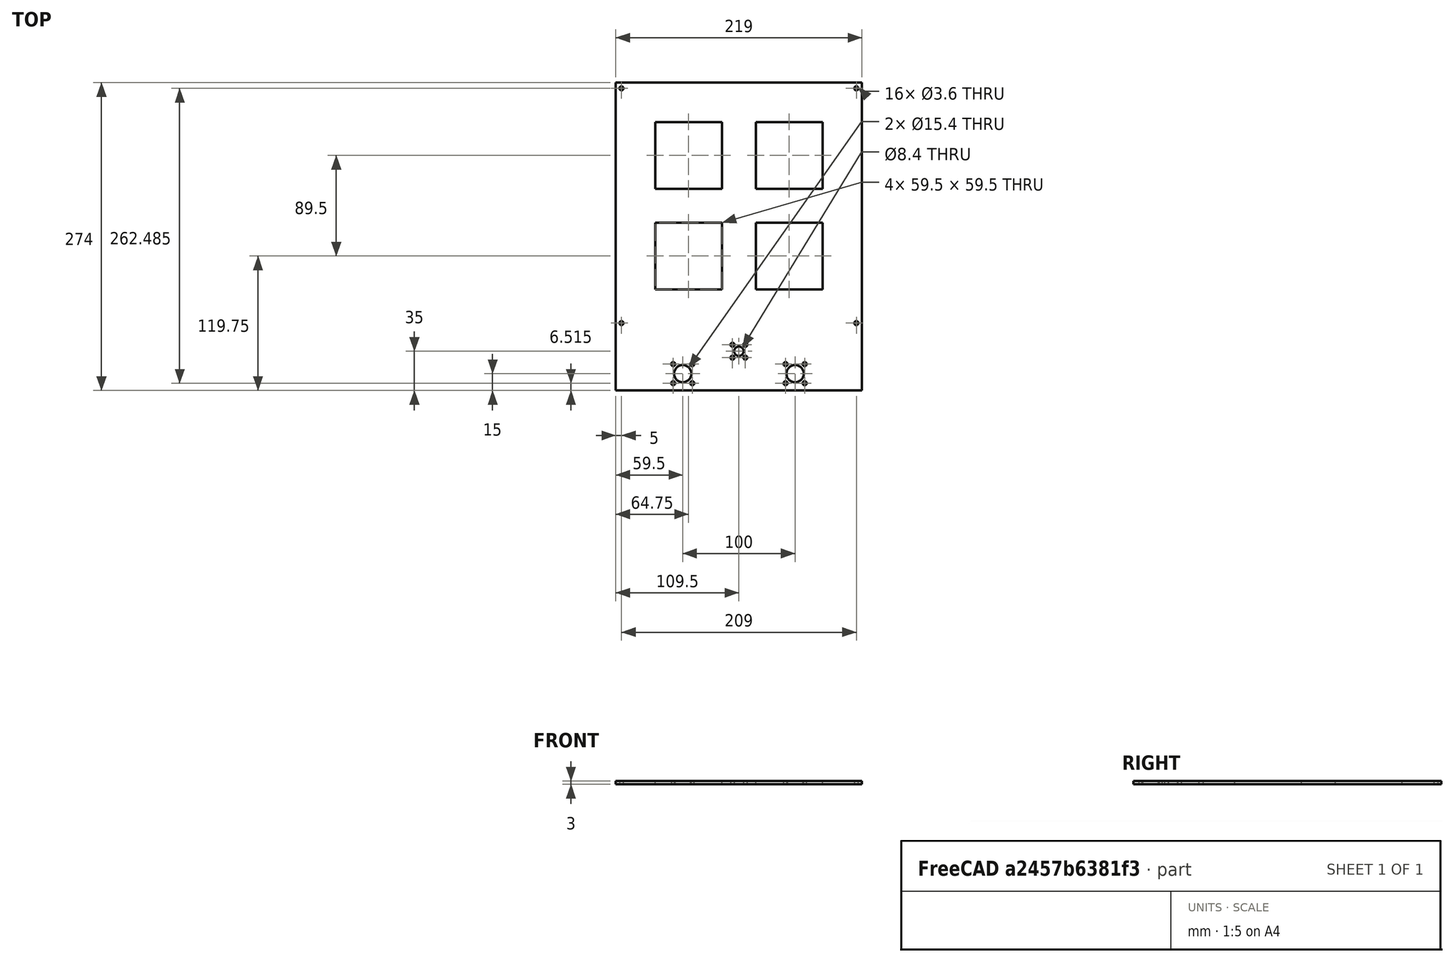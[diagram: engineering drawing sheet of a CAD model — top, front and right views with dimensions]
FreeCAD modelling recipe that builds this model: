
FCSTD DOCUMENT  (FreeCAD 0.16R6706 (Git))
Label: Suporte Mesa
License: All rights reserved
LicenseURL: http://en.wikipedia.org/wiki/All_rights_reserved
objects: Path::FeaturePython×26, Sketcher::SketchObject×1, PartDesign::Pad×1, Path::FeatureCompoundPython×1
note: 3 computed .brp shape members not serialized (recipe doc carries the construction recipe); baked Part::Feature solids carry a one-line shape summary decoded from their .brp

FEATURE [Sketcher::SketchObject] Sketch
  sketch-geometry (54):
    g0: LineSegment StartX=-109.5 StartY=274 StartZ=0 EndX=109.5 EndY=274 EndZ=0
    g1: LineSegment StartX=109.5 StartY=274 StartZ=0 EndX=109.5 EndY=0 EndZ=0
    g2: LineSegment StartX=109.5 StartY=0 StartZ=0 EndX=-109.5 EndY=0 EndZ=0
    g3: LineSegment StartX=-109.5 StartY=0 StartZ=0 EndX=-109.5 EndY=274 EndZ=0
    g4: LineSegment [constr] StartX=-104.5 StartY=269 StartZ=0 EndX=104.5 EndY=269 EndZ=0
    g5: LineSegment [constr] StartX=104.5 StartY=269 StartZ=0 EndX=104.5 EndY=60 EndZ=0
    g6: LineSegment [constr] StartX=104.5 StartY=60 StartZ=0 EndX=-104.5 EndY=60 EndZ=0
    g7: LineSegment [constr] StartX=-104.5 StartY=60 StartZ=0 EndX=-104.5 EndY=269 EndZ=0
    g8: Circle CenterX=-104.5 CenterY=60 CenterZ=0 NormalX=0 NormalY=0 NormalZ=1 Radius=1.8
    g9: Circle CenterX=104.5 CenterY=60 CenterZ=0 NormalX=0 NormalY=0 NormalZ=1 Radius=1.8
    g10: Circle CenterX=-104.5 CenterY=269 CenterZ=0 NormalX=0 NormalY=0 NormalZ=1 Radius=1.8
    g11: Circle CenterX=104.5 CenterY=269 CenterZ=0 NormalX=0 NormalY=0 NormalZ=1 Radius=1.8
    g12: LineSegment [constr] StartX=-50 StartY=15 StartZ=0 EndX=50 EndY=15 EndZ=0
    g13: Circle CenterX=0 CenterY=35 CenterZ=0 NormalX=0 NormalY=0 NormalZ=1 Radius=4.2
    g14: LineSegment [constr] StartX=-5.75 StartY=40.75 StartZ=0 EndX=5.75 EndY=40.75 EndZ=0
    g15: LineSegment [constr] StartX=5.75 StartY=40.75 StartZ=0 EndX=5.75 EndY=29.25 EndZ=0
    g16: LineSegment [constr] StartX=5.75 StartY=29.25 StartZ=0 EndX=-5.75 EndY=29.25 EndZ=0
    g17: LineSegment [constr] StartX=-5.75 StartY=29.25 StartZ=0 EndX=-5.75 EndY=40.75 EndZ=0
    g18: Circle CenterX=5.75 CenterY=29.25 CenterZ=0 NormalX=0 NormalY=0 NormalZ=1 Radius=1.8
    g19: Circle CenterX=5.75 CenterY=40.75 CenterZ=0 NormalX=0 NormalY=0 NormalZ=1 Radius=1.8
    g20: Circle CenterX=-5.75 CenterY=29.25 CenterZ=0 NormalX=0 NormalY=0 NormalZ=1 Radius=1.8
    g21: Circle CenterX=-5.75 CenterY=40.75 CenterZ=0 NormalX=0 NormalY=0 NormalZ=1 Radius=1.8
    g22: LineSegment [constr] StartX=-58.4853 StartY=6.51472 StartZ=0 EndX=-41.5147 EndY=23.4853 EndZ=0
    g23: GeomPoint [constr] X=-50 Y=15 Z=0
    g24: LineSegment [constr] StartX=-58.4853 StartY=23.4853 StartZ=0 EndX=-41.5147 EndY=6.51472 EndZ=0
    g25: Circle CenterX=-58.4853 CenterY=23.4853 CenterZ=0 NormalX=0 NormalY=0 NormalZ=1 Radius=1.8
    g26: Circle CenterX=-41.5147 CenterY=23.4853 CenterZ=0 NormalX=0 NormalY=0 NormalZ=1 Radius=1.8
    g27: Circle CenterX=-41.5147 CenterY=6.51472 CenterZ=0 NormalX=0 NormalY=0 NormalZ=1 Radius=1.8
    g28: Circle CenterX=-58.4853 CenterY=6.51472 CenterZ=0 NormalX=0 NormalY=0 NormalZ=1 Radius=1.8
    g29: Circle CenterX=-50 CenterY=15 CenterZ=0 NormalX=0 NormalY=0 NormalZ=1 Radius=7.7
    g30: LineSegment [constr] StartX=41.5147 StartY=6.51472 StartZ=0 EndX=58.4853 EndY=23.4853 EndZ=0
    g31: GeomPoint [constr] X=50 Y=15 Z=0
    g32: LineSegment [constr] StartX=41.5147 StartY=23.4853 StartZ=0 EndX=58.4853 EndY=6.51472 EndZ=0
    g33: Circle CenterX=41.5147 CenterY=23.4853 CenterZ=0 NormalX=0 NormalY=0 NormalZ=1 Radius=1.8
    g34: Circle CenterX=58.4853 CenterY=23.4853 CenterZ=0 NormalX=0 NormalY=0 NormalZ=1 Radius=1.8
    g35: Circle CenterX=58.4853 CenterY=6.51472 CenterZ=0 NormalX=0 NormalY=0 NormalZ=1 Radius=1.8
    g36: Circle CenterX=41.5147 CenterY=6.51472 CenterZ=0 NormalX=0 NormalY=0 NormalZ=1 Radius=1.8
    g37: Circle CenterX=50 CenterY=15 CenterZ=0 NormalX=0 NormalY=0 NormalZ=1 Radius=7.7
    g38: LineSegment StartX=-74.5 StartY=239 StartZ=0 EndX=-15 EndY=239 EndZ=0
    g39: LineSegment StartX=-15 StartY=239 StartZ=0 EndX=-15 EndY=179.5 EndZ=0
    g40: LineSegment StartX=-15 StartY=179.5 StartZ=0 EndX=-74.5 EndY=179.5 EndZ=0
    g41: LineSegment StartX=-74.5 StartY=179.5 StartZ=0 EndX=-74.5 EndY=239 EndZ=0
    g42: LineSegment StartX=15 StartY=239 StartZ=0 EndX=74.5 EndY=239 EndZ=0
    g43: LineSegment StartX=74.5 StartY=239 StartZ=0 EndX=74.5 EndY=179.5 EndZ=0
    g44: LineSegment StartX=74.5 StartY=179.5 StartZ=0 EndX=15 EndY=179.5 EndZ=0
    g45: LineSegment StartX=15 StartY=179.5 StartZ=0 EndX=15 EndY=239 EndZ=0
    g46: LineSegment StartX=15 StartY=149.5 StartZ=0 EndX=74.5 EndY=149.5 EndZ=0
    g47: LineSegment StartX=74.5 StartY=149.5 StartZ=0 EndX=74.5 EndY=90 EndZ=0
    g48: LineSegment StartX=74.5 StartY=90 StartZ=0 EndX=15 EndY=90 EndZ=0
    g49: LineSegment StartX=15 StartY=90 StartZ=0 EndX=15 EndY=149.5 EndZ=0
    g50: LineSegment StartX=-74.5 StartY=149.5 StartZ=0 EndX=-15 EndY=149.5 EndZ=0
    g51: LineSegment StartX=-15 StartY=149.5 StartZ=0 EndX=-15 EndY=90 EndZ=0
    g52: LineSegment StartX=-15 StartY=90 StartZ=0 EndX=-74.5 EndY=90 EndZ=0
    g53: LineSegment StartX=-74.5 StartY=90 StartZ=0 EndX=-74.5 EndY=149.5 EndZ=0
  constraints (138):
    c: Coincident(g0,g1)
    c: Coincident(g1,g2)
    c: Coincident(g2,g3)
    c: Coincident(g3,g0)
    c: Horizontal(g0)
    c: Horizontal(g2)
    c: Vertical(g1)
    c: Vertical(g3)
    c: DistanceX(g0,g0) = 219
    c: DistanceY(g1,g1) = 274
    c: Coincident(g4,g5)
    c: Coincident(g5,g6)
    c: Coincident(g6,g7)
    c: Coincident(g7,g4)
    c: Horizontal(g4)
    c: Horizontal(g6)
    c: Vertical(g5)
    c: Vertical(g7)
    c: DistanceX(g4,g4) = 209
    c: Equal(g4,g5)
    c: Radius(g8) = 1.8
    c: Equal(g8,g9) = 1.8
    c: Equal(g8,g10) = 1.8
    c: Equal(g8,g11) = 1.8
    c: Coincident(g6,g8)
    c: Coincident(g9,g5)
    c: Coincident(g11,g4)
    c: Coincident(g4,g10)
    c: Symmetric(g2,g1,g-1)
    c: Symmetric(g5,g6,g-2)
    c: DistanceY(g4,g0) = 5
    c: Horizontal(g12)
    c: Symmetric(g12,g12,g-2)
    c: PointOnObject(g13,g-2)
    c: DistanceY(g13,g5) = 25
    c: Radius(g13) = 4.2
    c: Coincident(g14,g15)
    c: Coincident(g15,g16)
    c: Coincident(g16,g17)
    c: Coincident(g17,g14)
    c: Horizontal(g14)
    c: Horizontal(g16)
    c: Vertical(g15)
    c: Vertical(g17)
    c: DistanceX(g14,g14) = 11.5
    c: Equal(g14,g15)
    c: Coincident(g14,g21)
    c: Coincident(g14,g19)
    c: Coincident(g18,g15)
    c: Coincident(g16,g20)
    c: Symmetric(g14,g16,g13)
    c: DistanceY(g1,g13) = 35
    c: DistanceY(g13,g0) = 239
    c: DistanceX(g12,g12) = 100
    c: DistanceX(g0,g4) = 5
    c: DistanceY(g12,g13) = 20
    c: Distance(g22) = 24
    c: Angle(g22) = 0.785398
    c: Symmetric(g22,g22,g23)
    c: Equal(g22,g24)
    c: Symmetric(g24,g24,g23)
    c: Perpendicular(g24,g22)
    c: Radius(g25) = 1.8
    c: Equal(g25,g26) = 1.8
    c: Equal(g25,g27) = 1.8
    c: Equal(g25,g28) = 1.8
    c: Coincident(g22,g28)
    c: Coincident(g24,g25)
    c: Coincident(g22,g26)
    c: Coincident(g24,g27)
    c: Radius(g29) = 7.7
    c: Coincident(g23,g29)
    c: Equal(g22,g30) = 24
    c: Parallel(g22,g30) = 0.785398
    c: Symmetric(g30,g30,g31)
    c: Equal(g30,g32)
    c: Symmetric(g32,g32,g31)
    c: Perpendicular(g32,g30)
    c: Equal(g25,g33) = 1.8
    c: Equal(g33,g34) = 1.8
    c: Equal(g33,g35) = 1.8
    c: Equal(g33,g36) = 1.8
    c: Coincident(g30,g36)
    c: Coincident(g32,g33)
    c: Coincident(g30,g34)
    c: Coincident(g32,g35)
    c: Equal(g29,g37) = 7.7
    c: Coincident(g31,g37)
    c: Coincident(g23,g12)
    c: Coincident(g31,g12)
    c: Coincident(g38,g39)
    c: Coincident(g39,g40)
    c: Coincident(g40,g41)
    c: Coincident(g41,g38)
    c: Horizontal(g38)
    c: Horizontal(g40)
    c: Vertical(g39)
    c: Vertical(g41)
    c: DistanceX(g38,g38) = 59.5
    c: Equal(g38,g41)
    c: Coincident(g42,g43)
    c: Coincident(g43,g44)
    c: Coincident(g44,g45)
    c: Coincident(g45,g42)
    c: Horizontal(g42)
    c: Horizontal(g44)
    c: Vertical(g43)
    c: Vertical(g45)
    c: Equal(g38,g42) = 59.5
    c: Equal(g42,g45)
    c: Coincident(g46,g47)
    c: Coincident(g47,g48)
    c: Coincident(g48,g49)
    c: Coincident(g49,g46)
    c: Horizontal(g46)
    c: Horizontal(g48)
    c: Vertical(g47)
    c: Vertical(g49)
    c: Equal(g38,g46) = 59.5
    c: Equal(g46,g49)
    c: Coincident(g50,g51)
    c: Coincident(g51,g52)
    c: Coincident(g52,g53)
    c: Coincident(g53,g50)
    c: Horizontal(g50)
    c: Horizontal(g52)
    c: Vertical(g51)
    c: Vertical(g53)
    c: Equal(g38,g50) = 59.5
    c: Equal(g50,g53)
    c: DistanceX(g4,g38) = 30
    c: DistanceY(g38,g4) = 30
    c: PointOnObject(g42,g38)
    c: DistanceX(g38,g42) = 30
    c: PointOnObject(g40,g53)
    c: DistanceY(g50,g40) = 30
    c: PointOnObject(g46,g50)
    c: PointOnObject(g46,g45)
FEATURE [PartDesign::Pad] Pad
  Length = 3
  Length2 = 100
  Sketch = -> Sketch
  Type = 0
FEATURE [Path::FeaturePython] Machine  label="Machine_"  # Path/CAM operation (typed FeaturePython)
  MachineUnits = 0
  X = 0
  X_Max = 0
  X_Min = 0
  Y = 0
  Y_Max = 0
  Y_Min = 0
  Z = 0
  Z_Max = 0
  Z_Min = 0
FEATURE [Path::FeaturePython] Tool  label="Tool1"  # Path/CAM operation (typed FeaturePython)
  SpindleDir = 0
  SpindleSpeed = 0
  ToolNumber = 1
FEATURE [Path::FeaturePython] Profile  label="conexao mesa"  # Path/CAM operation (typed FeaturePython)
  Active = true
  Base = -> Pad
  ClearanceHeight = 3
  Direction = 1
  Edge1 = -> Pad [Edge114]
  EndPoint = (0,0,0)
  ExtendAtEnd = 0
  ExtendAtStart = 0
  FinalDepth = -5.1
  HorizFeed = 127
  LeadInLineLen = 0
  LeadOutLineLen = 0
  OffsetExtra = 0
  PathClosed = true
  RetractHeight = 0
  RollRadius = 0
  SegLen = 0.5
  Side = 1
  StartDepth = 0
  StartPoint = (0,0,0)
  StepDown = 2
  ToolNumber = 1
  UseEndPoint = false
  UsePlacements = false
  UseStartDepth = true
  UseStartPoint = false
  VertFeed = 127
FEATURE [Path::FeaturePython] Profile001  label="conexao mesa001"  # Path/CAM operation (typed FeaturePython)
  Active = true
  Base = -> Pad
  ClearanceHeight = 3
  Direction = 1
  Edge1 = -> Pad [Edge117]
  EndPoint = (0,0,0)
  ExtendAtEnd = 0
  ExtendAtStart = 0
  FinalDepth = -5.1
  HorizFeed = 127
  LeadInLineLen = 0
  LeadOutLineLen = 0
  OffsetExtra = 0
  PathClosed = true
  RetractHeight = 0
  RollRadius = 0
  SegLen = 0.5
  Side = 1
  StartDepth = 0
  StartPoint = (0,0,0)
  StepDown = 2
  ToolNumber = 1
  UseEndPoint = false
  UsePlacements = false
  UseStartDepth = true
  UseStartPoint = false
  VertFeed = 127
FEATURE [Path::FeaturePython] Profile002  label="conexao mesa002"  # Path/CAM operation (typed FeaturePython)
  Active = true
  Base = -> Pad
  ClearanceHeight = 3
  Direction = 1
  Edge1 = -> Pad [Edge72]
  EndPoint = (0,0,0)
  ExtendAtEnd = 0
  ExtendAtStart = 0
  FinalDepth = -5.1
  HorizFeed = 127
  LeadInLineLen = 0
  LeadOutLineLen = 0
  OffsetExtra = 0
  PathClosed = true
  RetractHeight = 0
  RollRadius = 0
  SegLen = 0.5
  Side = 1
  StartDepth = 0
  StartPoint = (0,0,0)
  StepDown = 2
  ToolNumber = 1
  UseEndPoint = false
  UsePlacements = false
  UseStartDepth = true
  UseStartPoint = false
  VertFeed = 127
FEATURE [Path::FeaturePython] Profile003  label="conexao mesa003"  # Path/CAM operation (typed FeaturePython)
  Active = true
  Base = -> Pad
  ClearanceHeight = 3
  Direction = 1
  Edge1 = -> Pad [Edge75]
  EndPoint = (0,0,0)
  ExtendAtEnd = 0
  ExtendAtStart = 0
  FinalDepth = -5.1
  HorizFeed = 127
  LeadInLineLen = 0
  LeadOutLineLen = 0
  OffsetExtra = 0
  PathClosed = true
  RetractHeight = 0
  RollRadius = 0
  SegLen = 0.5
  Side = 1
  StartDepth = 0
  StartPoint = (0,0,0)
  StepDown = 2
  ToolNumber = 1
  UseEndPoint = false
  UsePlacements = false
  UseStartDepth = true
  UseStartPoint = false
  VertFeed = 127
FEATURE [Path::FeaturePython] Profile004  label="Eixos014"  # Path/CAM operation (typed FeaturePython)
  Active = true
  Base = -> Pad
  ClearanceHeight = 3
  Direction = 1
  Edge1 = -> Pad [Edge96]
  EndPoint = (0,0,0)
  ExtendAtEnd = 0
  ExtendAtStart = 0
  FinalDepth = -5.1
  HorizFeed = 127
  LeadInLineLen = 0
  LeadOutLineLen = 0
  OffsetExtra = 0
  PathClosed = true
  RetractHeight = 0
  RollRadius = 0
  SegLen = 0.5
  Side = 1
  StartDepth = 0
  StartPoint = (0,0,0)
  StepDown = 2
  ToolNumber = 1
  UseEndPoint = false
  UsePlacements = false
  UseStartDepth = true
  UseStartPoint = false
  VertFeed = 127
FEATURE [Path::FeaturePython] Profile005  label="Eixos013"  # Path/CAM operation (typed FeaturePython)
  Active = true
  Base = -> Pad
  ClearanceHeight = 3
  Direction = 1
  Edge1 = -> Pad [Edge87]
  EndPoint = (0,0,0)
  ExtendAtEnd = 0
  ExtendAtStart = 0
  FinalDepth = -5.1
  HorizFeed = 127
  LeadInLineLen = 0
  LeadOutLineLen = 0
  OffsetExtra = 0
  PathClosed = true
  RetractHeight = 0
  RollRadius = 0
  SegLen = 0.5
  Side = 1
  StartDepth = 0
  StartPoint = (0,0,0)
  StepDown = 2
  ToolNumber = 1
  UseEndPoint = false
  UsePlacements = false
  UseStartDepth = true
  UseStartPoint = false
  VertFeed = 127
FEATURE [Path::FeaturePython] Profile006  label="Eixos012"  # Path/CAM operation (typed FeaturePython)
  Active = true
  Base = -> Pad
  ClearanceHeight = 3
  Direction = 1
  Edge1 = -> Pad [Edge84]
  EndPoint = (0,0,0)
  ExtendAtEnd = 0
  ExtendAtStart = 0
  FinalDepth = -5.1
  HorizFeed = 127
  LeadInLineLen = 0
  LeadOutLineLen = 0
  OffsetExtra = 0
  PathClosed = true
  RetractHeight = 0
  RollRadius = 0
  SegLen = 0.5
  Side = 1
  StartDepth = 0
  StartPoint = (0,0,0)
  StepDown = 2
  ToolNumber = 1
  UseEndPoint = false
  UsePlacements = false
  UseStartDepth = true
  UseStartPoint = false
  VertFeed = 127
FEATURE [Path::FeaturePython] Profile007  label="Eixos011"  # Path/CAM operation (typed FeaturePython)
  Active = true
  Base = -> Pad
  ClearanceHeight = 3
  Direction = 1
  Edge1 = -> Pad [Edge99]
  EndPoint = (0,0,0)
  ExtendAtEnd = 0
  ExtendAtStart = 0
  FinalDepth = -5.1
  HorizFeed = 127
  LeadInLineLen = 0
  LeadOutLineLen = 0
  OffsetExtra = 0
  PathClosed = true
  RetractHeight = 0
  RollRadius = 0
  SegLen = 0.5
  Side = 1
  StartDepth = 0
  StartPoint = (0,0,0)
  StepDown = 2
  ToolNumber = 1
  UseEndPoint = false
  UsePlacements = false
  UseStartDepth = true
  UseStartPoint = false
  VertFeed = 127
FEATURE [Path::FeaturePython] Profile008  label="Eixos010"  # Path/CAM operation (typed FeaturePython)
  Active = true
  Base = -> Pad
  ClearanceHeight = 3
  Direction = 1
  Edge1 = -> Pad [Edge63]
  EndPoint = (0,0,0)
  ExtendAtEnd = 0
  ExtendAtStart = 0
  FinalDepth = -5.1
  HorizFeed = 127
  LeadInLineLen = 0
  LeadOutLineLen = 0
  OffsetExtra = 0
  PathClosed = true
  RetractHeight = 0
  RollRadius = 0
  SegLen = 0.5
  Side = 1
  StartDepth = 0
  StartPoint = (0,0,0)
  StepDown = 2
  ToolNumber = 1
  UseEndPoint = false
  UsePlacements = false
  UseStartDepth = true
  UseStartPoint = false
  VertFeed = 127
FEATURE [Path::FeaturePython] Profile009  label="Eixos009"  # Path/CAM operation (typed FeaturePython)
  Active = true
  Base = -> Pad
  ClearanceHeight = 3
  Direction = 1
  Edge1 = -> Pad [Edge81]
  EndPoint = (0,0,0)
  ExtendAtEnd = 0
  ExtendAtStart = 0
  FinalDepth = -5.1
  HorizFeed = 127
  LeadInLineLen = 0
  LeadOutLineLen = 0
  OffsetExtra = 0
  PathClosed = true
  RetractHeight = 0
  RollRadius = 0
  SegLen = 0.5
  Side = 1
  StartDepth = 0
  StartPoint = (0,0,0)
  StepDown = 2
  ToolNumber = 1
  UseEndPoint = false
  UsePlacements = false
  UseStartDepth = true
  UseStartPoint = false
  VertFeed = 127
FEATURE [Path::FeaturePython] Profile010  label="Eixos008"  # Path/CAM operation (typed FeaturePython)
  Active = true
  Base = -> Pad
  ClearanceHeight = 3
  Direction = 1
  Edge1 = -> Pad [Edge111]
  EndPoint = (0,0,0)
  ExtendAtEnd = 0
  ExtendAtStart = 0
  FinalDepth = -5.1
  HorizFeed = 127
  LeadInLineLen = 0
  LeadOutLineLen = 0
  OffsetExtra = 0
  PathClosed = true
  RetractHeight = 0
  RollRadius = 0
  SegLen = 0.5
  Side = 1
  StartDepth = 0
  StartPoint = (0,0,0)
  StepDown = 2
  ToolNumber = 1
  UseEndPoint = false
  UsePlacements = false
  UseStartDepth = true
  UseStartPoint = false
  VertFeed = 127
FEATURE [Path::FeaturePython] Profile011  label="Eixos007"  # Path/CAM operation (typed FeaturePython)
  Active = true
  Base = -> Pad
  ClearanceHeight = 3
  Direction = 1
  Edge1 = -> Pad [Edge69]
  EndPoint = (0,0,0)
  ExtendAtEnd = 0
  ExtendAtStart = 0
  FinalDepth = -5.1
  HorizFeed = 127
  LeadInLineLen = 0
  LeadOutLineLen = 0
  OffsetExtra = 0
  PathClosed = true
  RetractHeight = 0
  RollRadius = 0
  SegLen = 0.5
  Side = 1
  StartDepth = 0
  StartPoint = (0,0,0)
  StepDown = 2
  ToolNumber = 1
  UseEndPoint = false
  UsePlacements = false
  UseStartDepth = true
  UseStartPoint = false
  VertFeed = 127
FEATURE [Path::FeaturePython] Profile012  label="Eixos006"  # Path/CAM operation (typed FeaturePython)
  Active = true
  Base = -> Pad
  ClearanceHeight = 3
  Direction = 1
  Edge1 = -> Pad [Edge78]
  EndPoint = (0,0,0)
  ExtendAtEnd = 0
  ExtendAtStart = 0
  FinalDepth = -5.1
  HorizFeed = 127
  LeadInLineLen = 0
  LeadOutLineLen = 0
  OffsetExtra = 0
  PathClosed = true
  RetractHeight = 0
  RollRadius = 0
  SegLen = 0.5
  Side = 1
  StartDepth = 0
  StartPoint = (0,0,0)
  StepDown = 2
  ToolNumber = 1
  UseEndPoint = false
  UsePlacements = false
  UseStartDepth = true
  UseStartPoint = false
  VertFeed = 127
FEATURE [Path::FeaturePython] Profile013  label="Eixos005"  # Path/CAM operation (typed FeaturePython)
  Active = true
  Base = -> Pad
  ClearanceHeight = 3
  Direction = 1
  Edge1 = -> Pad [Edge108]
  EndPoint = (0,0,0)
  ExtendAtEnd = 0
  ExtendAtStart = 0
  FinalDepth = -5.1
  HorizFeed = 127
  LeadInLineLen = 0
  LeadOutLineLen = 0
  OffsetExtra = 0
  PathClosed = true
  RetractHeight = 0
  RollRadius = 0
  SegLen = 0.5
  Side = 1
  StartDepth = 0
  StartPoint = (0,0,0)
  StepDown = 2
  ToolNumber = 1
  UseEndPoint = false
  UsePlacements = false
  UseStartDepth = true
  UseStartPoint = false
  VertFeed = 127
FEATURE [Path::FeaturePython] Profile014  label="Eixos004"  # Path/CAM operation (typed FeaturePython)
  Active = true
  Base = -> Pad
  ClearanceHeight = 3
  Direction = 1
  Edge1 = -> Pad [Edge102]
  EndPoint = (0,0,0)
  ExtendAtEnd = 0
  ExtendAtStart = 0
  FinalDepth = -5.1
  HorizFeed = 127
  LeadInLineLen = 0
  LeadOutLineLen = 0
  OffsetExtra = 0
  PathClosed = true
  RetractHeight = 0
  RollRadius = 0
  SegLen = 0.5
  Side = 1
  StartDepth = 0
  StartPoint = (0,0,0)
  StepDown = 2
  ToolNumber = 1
  UseEndPoint = false
  UsePlacements = false
  UseStartDepth = true
  UseStartPoint = false
  VertFeed = 127
FEATURE [Path::FeaturePython] Profile015  label="Eixos003"  # Path/CAM operation (typed FeaturePython)
  Active = true
  Base = -> Pad
  ClearanceHeight = 3
  Direction = 1
  Edge1 = -> Pad [Edge93]
  EndPoint = (0,0,0)
  ExtendAtEnd = 0
  ExtendAtStart = 0
  FinalDepth = -5.1
  HorizFeed = 127
  LeadInLineLen = 0
  LeadOutLineLen = 0
  OffsetExtra = 0
  PathClosed = true
  RetractHeight = 0
  RollRadius = 0
  SegLen = 0.5
  Side = 1
  StartDepth = 0
  StartPoint = (0,0,0)
  StepDown = 2
  ToolNumber = 1
  UseEndPoint = false
  UsePlacements = false
  UseStartDepth = true
  UseStartPoint = false
  VertFeed = 127
FEATURE [Path::FeaturePython] Profile016  label="Eixos002"  # Path/CAM operation (typed FeaturePython)
  Active = true
  Base = -> Pad
  ClearanceHeight = 3
  Direction = 1
  Edge1 = -> Pad [Edge90]
  EndPoint = (0,0,0)
  ExtendAtEnd = 0
  ExtendAtStart = 0
  FinalDepth = -5.1
  HorizFeed = 127
  LeadInLineLen = 0
  LeadOutLineLen = 0
  OffsetExtra = 0
  PathClosed = true
  RetractHeight = 0
  RollRadius = 0
  SegLen = 0.5
  Side = 1
  StartDepth = 0
  StartPoint = (0,0,0)
  StepDown = 2
  ToolNumber = 1
  UseEndPoint = false
  UsePlacements = false
  UseStartDepth = true
  UseStartPoint = false
  VertFeed = 127
FEATURE [Path::FeaturePython] Profile017  label="Eixos001"  # Path/CAM operation (typed FeaturePython)
  Active = true
  Base = -> Pad
  ClearanceHeight = 3
  Direction = 1
  Edge1 = -> Pad [Edge105]
  EndPoint = (0,0,0)
  ExtendAtEnd = 0
  ExtendAtStart = 0
  FinalDepth = -5.1
  HorizFeed = 127
  LeadInLineLen = 0
  LeadOutLineLen = 0
  OffsetExtra = 0
  PathClosed = true
  RetractHeight = 0
  RollRadius = 0
  SegLen = 0.5
  Side = 1
  StartDepth = 0
  StartPoint = (0,0,0)
  StepDown = 2
  ToolNumber = 1
  UseEndPoint = false
  UsePlacements = false
  UseStartDepth = true
  UseStartPoint = false
  VertFeed = 127
FEATURE [Path::FeaturePython] Profile018  label="Eixos"  # Path/CAM operation (typed FeaturePython)
  Active = true
  Base = -> Pad
  ClearanceHeight = 3
  Direction = 1
  Edge1 = -> Pad [Edge66]
  EndPoint = (0,0,0)
  ExtendAtEnd = 0
  ExtendAtStart = 0
  FinalDepth = -5.1
  HorizFeed = 127
  LeadInLineLen = 0
  LeadOutLineLen = 0
  OffsetExtra = 0
  PathClosed = true
  RetractHeight = 0
  RollRadius = 0
  SegLen = 0.5
  Side = 1
  StartDepth = 0
  StartPoint = (0,0,0)
  StepDown = 2
  ToolNumber = 1
  UseEndPoint = false
  UsePlacements = false
  UseStartDepth = true
  UseStartPoint = false
  VertFeed = 127
FEATURE [Path::FeaturePython] Profile019  label="Janelas"  # Path/CAM operation (typed FeaturePython)
  Active = true
  Base = -> Pad
  ClearanceHeight = 3
  Direction = 1
  Edge1 = -> Pad [Edge28]
  Edge2 = -> Pad [Edge36]
  EndPoint = (0,0,0)
  ExtendAtEnd = 0
  ExtendAtStart = 0
  FinalDepth = -5.1
  HorizFeed = 127
  LeadInLineLen = 0
  LeadOutLineLen = 0
  OffsetExtra = 0
  PathClosed = true
  RetractHeight = 0
  RollRadius = 0
  SegLen = 0.5
  Side = 1
  StartDepth = 0
  StartPoint = (0,0,0)
  StepDown = 2
  ToolNumber = 1
  UseEndPoint = false
  UsePlacements = false
  UseStartDepth = true
  UseStartPoint = false
  VertFeed = 127
FEATURE [Path::FeaturePython] Profile020  label="Janelas001"  # Path/CAM operation (typed FeaturePython)
  Active = true
  Base = -> Pad
  ClearanceHeight = 3
  Direction = 1
  Edge1 = -> Pad [Edge52]
  Edge2 = -> Pad [Edge60]
  EndPoint = (0,0,0)
  ExtendAtEnd = 0
  ExtendAtStart = 0
  FinalDepth = -5.1
  HorizFeed = 127
  LeadInLineLen = 0
  LeadOutLineLen = 0
  OffsetExtra = 0
  PathClosed = true
  RetractHeight = 0
  RollRadius = 0
  SegLen = 0.5
  Side = 1
  StartDepth = 0
  StartPoint = (0,0,0)
  StepDown = 2
  ToolNumber = 1
  UseEndPoint = false
  UsePlacements = false
  UseStartDepth = true
  UseStartPoint = false
  VertFeed = 127
FEATURE [Path::FeaturePython] Profile021  label="Janelas002"  # Path/CAM operation (typed FeaturePython)
  Active = true
  Base = -> Pad
  ClearanceHeight = 3
  Direction = 1
  Edge1 = -> Pad [Edge22]
  Edge2 = -> Pad [Edge18]
  EndPoint = (0,0,0)
  ExtendAtEnd = 0
  ExtendAtStart = 0
  FinalDepth = -5.1
  HorizFeed = 127
  LeadInLineLen = 0
  LeadOutLineLen = 0
  OffsetExtra = 0
  PathClosed = true
  RetractHeight = 0
  RollRadius = 0
  SegLen = 0.5
  Side = 1
  StartDepth = 0
  StartPoint = (0,0,0)
  StepDown = 2
  ToolNumber = 1
  UseEndPoint = false
  UsePlacements = false
  UseStartDepth = true
  UseStartPoint = false
  VertFeed = 127
FEATURE [Path::FeaturePython] Profile022  label="Janelas003"  # Path/CAM operation (typed FeaturePython)
  Active = true
  Base = -> Pad
  ClearanceHeight = 3
  Direction = 1
  Edge1 = -> Pad [Edge40]
  Edge2 = -> Pad [Edge48]
  EndPoint = (0,0,0)
  ExtendAtEnd = 0
  ExtendAtStart = 0
  FinalDepth = -5.1
  HorizFeed = 127
  LeadInLineLen = 0
  LeadOutLineLen = 0
  OffsetExtra = 0
  PathClosed = true
  RetractHeight = 0
  RollRadius = 0
  SegLen = 0.5
  Side = 1
  StartDepth = 0
  StartPoint = (0,0,0)
  StepDown = 2
  ToolNumber = 1
  UseEndPoint = false
  UsePlacements = false
  UseStartDepth = true
  UseStartPoint = false
  VertFeed = 127
FEATURE [Path::FeaturePython] Profile023  label="Externo"  # Path/CAM operation (typed FeaturePython)
  Active = true
  Base = -> Pad
  ClearanceHeight = 3
  Direction = 0
  EndPoint = (0,0,0)
  ExtendAtEnd = 0
  ExtendAtStart = 0
  Face1 = -> Pad [Face41]
  FinalDepth = -5.1
  HorizFeed = 127
  LeadInLineLen = 0
  LeadOutLineLen = 0
  OffsetExtra = 0
  PathClosed = true
  RetractHeight = 0
  RollRadius = 0
  SegLen = 0.5
  Side = 0
  StartDepth = 0
  StartPoint = (0,0,0)
  StepDown = 2
  ToolNumber = 1
  UseEndPoint = false
  UsePlacements = false
  UseStartDepth = true
  UseStartPoint = false
  VertFeed = 127
FEATURE [Path::FeatureCompoundPython] Project  # Path/CAM operation (typed FeaturePython)
  Group = -> [Machine,Tool,Profile,Profile001,Profile002,Profile003,Profile004,Profile005,Profile006,Profile007,Profile008,Profile009,Profile010,Profile011,Profile012,Profile013,Profile014,Profile015,Profile016,Profile017,Profile018,Profile019,Profile020,Profile021,Profile022,Profile023]
  UsePlacements = false
